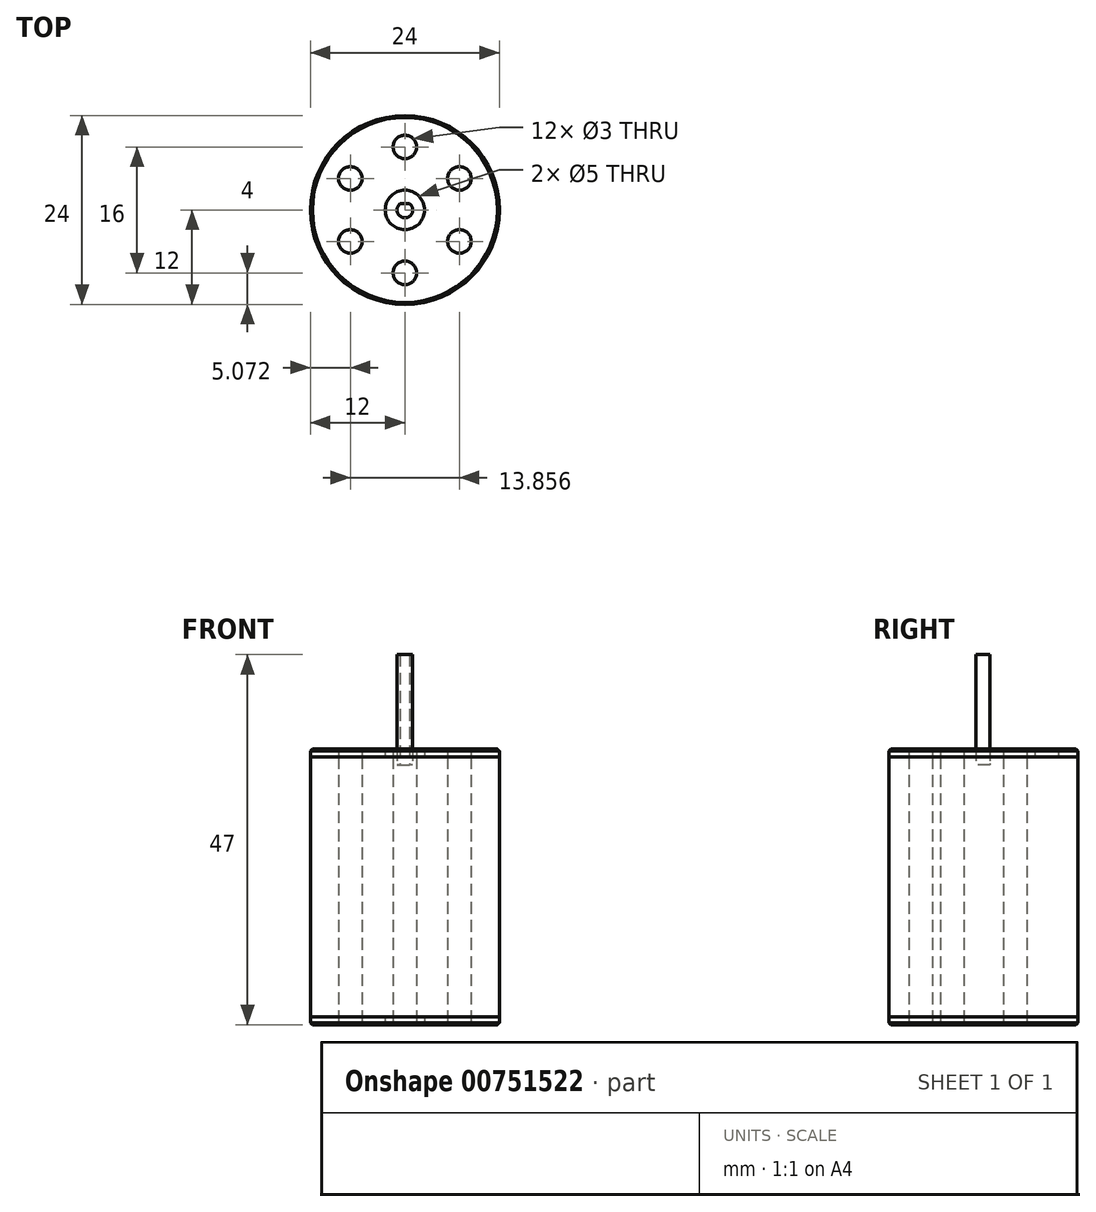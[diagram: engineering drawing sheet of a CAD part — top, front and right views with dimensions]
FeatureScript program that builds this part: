
annotation { "Feature Type Name" : "Feature", "Feature Type Description" : "" }
export const myFeature = defineFeature(function(context is Context, id is Id, definition is map)
    precondition{}
    {
        {
            var Q0;
            Q0=qCreatedBy(makeId("Top.planeOp"),FACE);
            var sketch = newSketch(context, id + "F0", { "sketchPlane" : qUnion([Q0])});
            skCircle(sketch, "E0", {"center": v(0, 0) * mm, "radius": 12 * mm});
            skCircle(sketch, "E1", {"center": v(0, 8) * mm, "radius": 1.5 * mm});
            skCircle(sketch, "E2", {"center": v(0, 0) * mm, "radius": 1 * mm});
            skLineSegment(sketch, "E3", {"start": v(-0.6, 0.8) * mm, "end": v(0.6, 0.8) * mm});
            skCircle(sketch, "E4", {"center": v(0, 0) * mm, "radius": 2.5 * mm});
            skCircle(sketch, "E5.MirrorC", {"center": v(0, -8) * mm, "radius": 1.5 * mm});
            skLineSegment(sketch, "E6", {"start": v(0, 0) * mm, "end": v(10.95, 10.95) * mm, "construction": true});
            skCircle(sketch, "E7", {"center": v(-6.93, 4) * mm, "radius": 1.5 * mm});
            skCircle(sketch, "E8", {"center": v(6.93, -4) * mm, "radius": 1.5 * mm});
            skLineSegment(sketch, "E9", {"start": v(6.93, -4) * mm, "end": v(-6.93, 4) * mm, "construction": true});
            skCircle(sketch, "E10.MirrorC", {"center": v(6.93, 4) * mm, "radius": 1.5 * mm});
            skCircle(sketch, "E11.MirrorC", {"center": v(-6.93, -4) * mm, "radius": 1.5 * mm});
            skSolve(sketch);
        }
        {
            var Q0;
            Q0=makeQuery(id+"F0.imprint","IMPRINT",FACE,{"disambiguationData":[TD([[makeQuery(id+"F0.imprint","IMPRINT",EDGE,{"derivedFrom":sQuery(id+"F0.wireOp",EDGE,"E7")}),1.0]])]});
            var Q1;
            Q1=makeQuery(id+"F0.imprint","IMPRINT",FACE,{"disambiguationData":[TD([[makeQuery(id+"F0.imprint","IMPRINT",EDGE,{"derivedFrom":sQuery(id+"F0.wireOp",EDGE,"E11.MirrorC")}),-1.0]])]});
            var Q2;
            Q2=makeQuery(id+"F0.imprint","IMPRINT",FACE,{"disambiguationData":[TD([[makeQuery(id+"F0.imprint","IMPRINT",EDGE,{"derivedFrom":sQuery(id+"F0.wireOp",EDGE,"E5.MirrorC")}),-1.0]])]});
            var Q3;
            Q3=makeQuery(id+"F0.imprint","IMPRINT",FACE,{"disambiguationData":[TD([[makeQuery(id+"F0.imprint","IMPRINT",EDGE,{"derivedFrom":sQuery(id+"F0.wireOp",EDGE,"E8")}),1.0]])]});
            var Q4;
            Q4=makeQuery(id+"F0.imprint","IMPRINT",FACE,{"disambiguationData":[TD([[makeQuery(id+"F0.imprint","IMPRINT",EDGE,{"derivedFrom":sQuery(id+"F0.wireOp",EDGE,"E10.MirrorC")}),-1.0]])]});
            var Q5;
            Q5=makeQuery(id+"F0.imprint","IMPRINT",FACE,{"disambiguationData":[TD([[makeQuery(id+"F0.imprint","IMPRINT",EDGE,{"derivedFrom":sQuery(id+"F0.wireOp",EDGE,"E1")}),1.0]])]});
            var Q6;
            Q6=makeQuery(id+"F0.imprint","IMPRINT",FACE,{"disambiguationData":[TD([[makeQuery(id+"F0.imprint","IMPRINT",EDGE,{"derivedFrom":sQuery(id+"F0.wireOp",EDGE,"E0")}),1.0]])]});
            extrude(context, id + "F1", {"entities" : qUnion([Q0, Q1, Q2, Q3, Q4, Q5, Q6]), "depth" : 1 * mm, "offsetDistance" : 25 * mm});
        }
        {
            var Q0;
            Q0=makeQuery(id+"F0.imprint","IMPRINT",FACE,{"disambiguationData":[TD([[makeQuery(id+"F0.imprint","IMPRINT",EDGE,{"derivedFrom":sQuery(id+"F0.wireOp",EDGE,"E11.MirrorC")}),-1.0]])]});
            var Q1;
            Q1=makeQuery(id+"F0.imprint","IMPRINT",FACE,{"disambiguationData":[TD([[makeQuery(id+"F0.imprint","IMPRINT",EDGE,{"derivedFrom":sQuery(id+"F0.wireOp",EDGE,"E5.MirrorC")}),-1.0]])]});
            var Q2;
            Q2=makeQuery(id+"F0.imprint","IMPRINT",FACE,{"disambiguationData":[TD([[makeQuery(id+"F0.imprint","IMPRINT",EDGE,{"derivedFrom":sQuery(id+"F0.wireOp",EDGE,"E10.MirrorC")}),-1.0]])]});
            var Q3;
            Q3=makeQuery(id+"F0.imprint","IMPRINT",FACE,{"disambiguationData":[TD([[makeQuery(id+"F0.imprint","IMPRINT",EDGE,{"derivedFrom":sQuery(id+"F0.wireOp",EDGE,"E8")}),1.0]])]});
            var Q4;
            Q4=makeQuery(id+"F0.imprint","IMPRINT",FACE,{"disambiguationData":[TD([[makeQuery(id+"F0.imprint","IMPRINT",EDGE,{"derivedFrom":sQuery(id+"F0.wireOp",EDGE,"E0")}),1.0]])]});
            var Q5;
            Q5=makeQuery(id+"F0.imprint","IMPRINT",FACE,{"disambiguationData":[TD([[makeQuery(id+"F0.imprint","IMPRINT",EDGE,{"derivedFrom":sQuery(id+"F0.wireOp",EDGE,"E1")}),1.0]])]});
            var Q6;
            Q6=makeQuery(id+"F0.imprint","IMPRINT",FACE,{"disambiguationData":[TD([[makeQuery(id+"F0.imprint","IMPRINT",EDGE,{"derivedFrom":sQuery(id+"F0.wireOp",EDGE,"E7")}),1.0]])]});
            var Q7;
            Q7=makeQuery(id+"F0.imprint","IMPRINT",FACE,{"disambiguationData":[TD([[makeQuery(id+"F0.imprint","IMPRINT",EDGE,{"derivedFrom":sQuery(id+"F0.wireOp",EDGE,"E4")}),1.0]])]});
            var Q8;
            {var subQ0=sQuery(id+"F0.wireOp",EDGE,"E3");Q8=makeQuery(id+"F0.imprint","IMPRINT",FACE,{"disambiguationData":[TD([[makeQuery(id+"F0.imprint","IMPRINT",EDGE,{"derivedFrom":subQ0}),-1.0]])]});}
            var Q9;
            {var subQ0=sQuery(id+"F0.wireOp",EDGE,"E3");Q9=makeQuery(id+"F0.imprint","IMPRINT",FACE,{"disambiguationData":[TD([[makeQuery(id+"F0.imprint","IMPRINT",EDGE,{"derivedFrom":subQ0}),1.0]])]});}
            extrude(context, id + "F2", {"entities" : qUnion([Q0, Q1, Q2, Q3, Q4, Q5, Q6, Q7, Q8, Q9]), "depth" : 34 * mm, "offsetDistance" : 25 * mm, "hasSecondDirection" : true, "secondDirectionOppositeDirection" : false, "secondDirectionDepth" : 1 * mm});
        }
        {
            var Q0;
            Q0=makeQuery(id+"F0.imprint","IMPRINT",FACE,{"disambiguationData":[TD([[makeQuery(id+"F0.imprint","IMPRINT",EDGE,{"derivedFrom":sQuery(id+"F0.wireOp",EDGE,"E0")}),1.0]])]});
            extrude(context, id + "F3", {"entities" : qUnion([Q0]), "depth" : 35 * mm, "offsetDistance" : 25 * mm, "hasSecondDirection" : true, "secondDirectionOppositeDirection" : false, "secondDirectionDepth" : 34 * mm});
        }
        {
            var Q0;
            {var subQ0=sQuery(id+"F0.wireOp",EDGE,"E3");Q0=makeQuery(id+"F0.imprint","IMPRINT",FACE,{"disambiguationData":[TD([[makeQuery(id+"F0.imprint","IMPRINT",EDGE,{"derivedFrom":subQ0}),-1.0]])]});}
            extrude(context, id + "F4", {"entities" : qUnion([Q0]), "depth" : 47 * mm, "offsetDistance" : 25 * mm, "hasSecondDirection" : true, "secondDirectionOppositeDirection" : false, "secondDirectionDepth" : 33 * mm});
        }
        {
            var Q0;
            Q0=makeQuery(id+"F3.opExtrude","CAP_EDGE",EDGE,{"disambiguationData":[OSD([sQuery(id+"F0.wireOp",EDGE,"E0")])],"isStart":false});
            var Q1;
            Q1=makeQuery(id+"F1.opExtrude","CAP_EDGE",EDGE,{"disambiguationData":[OSD([sQuery(id+"F0.wireOp",EDGE,"E0")])],"isStart":true});
            chamfer(context, id + "F5", {"entities" : qUnion([Q0, Q1]), "width" : .25 * mm, "tangentPropagation" : true});
        }
    });
